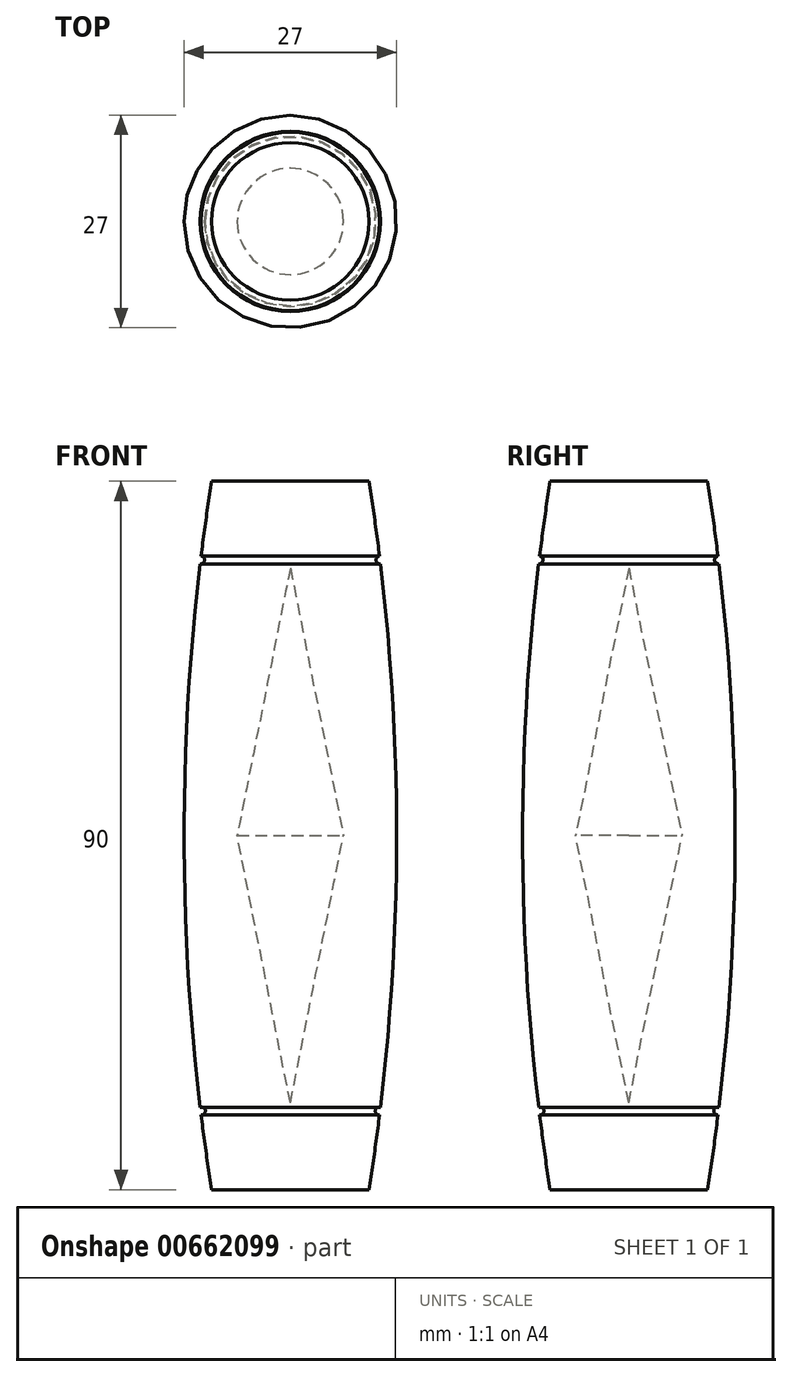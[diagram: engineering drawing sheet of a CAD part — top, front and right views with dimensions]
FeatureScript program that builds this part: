
annotation { "Feature Type Name" : "Feature", "Feature Type Description" : "" }
export const myFeature = defineFeature(function(context is Context, id is Id, definition is map)
    precondition{}
    {
        {
            var Q0;
            Q0=qCreatedBy(makeId("Front.planeOp"),FACE);
            var sketch = newSketch(context, id + "F0", { "sketchPlane" : qUnion([Q0])});
            skLineSegment(sketch, "E0", {"start": v(0, 0) * mm, "end": v(0, 90) * mm});
            skLineSegment(sketch, "E1", {"start": v(0, 0) * mm, "end": v(10, 0) * mm});
            skLineSegment(sketch, "E2", {"start": v(0, 0) * mm, "end": v(-10, 0) * mm});
            skLineSegment(sketch, "E3", {"start": v(0, 90) * mm, "end": v(-10, 90) * mm});
            skLineSegment(sketch, "E4", {"start": v(0, 90) * mm, "end": v(10, 90) * mm});
            skLineSegment(sketch, "E5", {"start": v(10, 0) * mm, "end": v(10, 90) * mm});
            skArc(sketch, "E6", {"start": v(-10, 90) * mm, "mid": v(-13.5, 45) * mm, "end": v(-10, 0) * mm});
            skArc(sketch, "E7", {"start": v(10, 0) * mm, "mid": v(13.5, 45) * mm, "end": v(10, 90) * mm});
            skPoint(sketch, "E8", {"position": v(0, 45) * mm});
            skLineSegment(sketch, "E9", {"start": v(0, 45) * mm, "end": v(13.5, 45) * mm});
            skPoint(sketch, "E10", {"position": v(-10, 10) * mm});
            skPoint(sketch, "E11", {"position": v(-10, 80) * mm});
            skLineSegment(sketch, "E12", {"start": v(-10, 80) * mm, "end": v(-11.39, 80) * mm});
            skCircle(sketch, "E13", {"center": v(-11.39, 80) * mm, "radius": 0.5 * mm});
            skPoint(sketch, "E14", {"position": v(-11.29, 10) * mm});
            skCircle(sketch, "E15", {"center": v(-11.29, 10) * mm, "radius": 0.5 * mm});
            skPoint(sketch, "E16", {"position": v(0, 11) * mm});
            skPoint(sketch, "E17", {"position": v(0, 79) * mm});
            skPoint(sketch, "E18", {"position": v(6.75, 45) * mm});
            skLineSegment(sketch, "E19", {"start": v(0, 11) * mm, "end": v(6.75, 45) * mm});
            skLineSegment(sketch, "E20", {"start": v(6.75, 45) * mm, "end": v(0, 79) * mm});
            skPoint(sketch, "E21", {"position": v(-6.75, 45) * mm});
            skLineSegment(sketch, "E22", {"start": v(0, 11) * mm, "end": v(-6.75, 45) * mm});
            skLineSegment(sketch, "E23", {"start": v(-6.75, 45) * mm, "end": v(0, 79) * mm});
            skSolve(sketch);
        }
        {
            var Q0;
            {var subQ7=sQuery(id+"F0.wireOp",EDGE,"E2");Q0=makeQuery(id+"F0.imprint","IMPRINT",FACE,{"disambiguationData":[TD([[makeQuery(id+"F0.imprint","IMPRINT",EDGE,{"derivedFrom":subQ7}),-1.0]])]});}
            var Q1;
            Q1=sQuery(id+"F0.wireOp",EDGE,"E0");
            revolve(context, id + "F1", {"surfaceOperationType" : NewSurfaceOperationType.NEW, "entities" : qUnion([Q0]), "axis" : qUnion([Q1]), "revolveType" : RevolveType.FULL});
        }
    });
